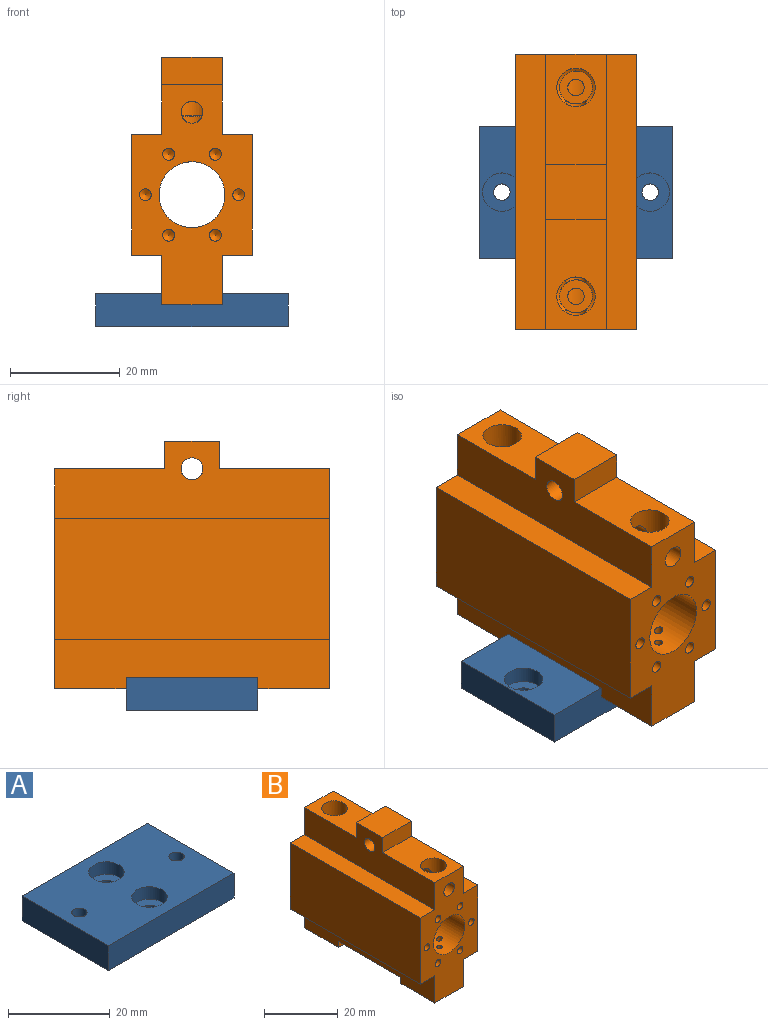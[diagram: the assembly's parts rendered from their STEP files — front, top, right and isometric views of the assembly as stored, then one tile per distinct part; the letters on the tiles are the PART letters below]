
ASSEMBLY  parts=2 mates=1
PART A: 18 faces, bbox 35x24x6 mm
  f0: plane 24x6mm, normal (-1,0,0), area 144mm2, adj f1,f3,f4,f5
  f1: plane 35x6mm, normal (0,-1,0), area 210mm2, adj f0,f2,f4,f5
  f2: plane 24x6mm, normal (1,0,0), area 144mm2, adj f1,f3,f4,f5
  f3: plane 35x6mm, normal (0,1,0), area 210mm2, adj f0,f2,f4,f5
  f4: plane 35x24mm, normal (0,0,1), area 748.9mm2, adj f0,f1,f2,f3,f8,f11,f12,f15
  f5: plane 35x24mm, normal (0,0,-1), area 748.9mm2, adj f0,f1,f2,f3,f6,f9,f14,f17
  f6: cylinder r=1.5mm len=3mm, axis (0,0,1), area 28.3mm2, adj f5,f7
  f7: plane 7x7mm, normal (0,0,1), area 31.4mm2, adj f6,f8
  f8: cylinder r=3.5mm len=7mm, axis (0,0,1), area 66mm2, adj f4,f7
  f9: cylinder r=1.5mm len=3mm, axis (0,0,1), area 28.3mm2, adj f5,f10
  f10: plane 7x7mm, normal (0,0,1), area 31.4mm2, adj f9,f11
  f11: cylinder r=3.5mm len=7mm, axis (0,0,1), area 66mm2, adj f4,f10
  f12: cylinder r=1.5mm len=3mm, axis (0,0,-1), area 28.3mm2, adj f4,f13
  f13: plane 7x7mm, normal (0,0,-1), area 31.4mm2, adj f12,f14
  f14: cylinder r=3.5mm len=7mm, axis (0,0,-1), area 66mm2, adj f5,f13
  f15: cylinder r=1.5mm len=3mm, axis (0,0,-1), area 28.3mm2, adj f4,f16
  f16: plane 7x7mm, normal (0,0,-1), area 31.4mm2, adj f15,f17
  f17: cylinder r=3.5mm len=7mm, axis (0,0,-1), area 66mm2, adj f5,f16
PART B: 77 faces, bbox 22x50x45 mm
  f0: cylinder r=0.75mm len=6.5mm, axis (0,0,-1), area 27.1mm2, adj f22,f76
  f1: cylinder r=0.75mm len=5.75mm, axis (0,0,-1), area 25mm2, adj f22,f76
  f2: cylinder r=0.75mm len=6.5mm, axis (0,0,-1), area 27.1mm2, adj f22,f76
  f3: cylinder r=0.75mm len=5.75mm, axis (0,0,-1), area 25mm2, adj f22,f76
  f4: cylinder r=0.75mm len=6.5mm, axis (0,0,-1), area 27.1mm2, adj f21,f76
  f5: cylinder r=0.75mm len=5.75mm, axis (0,0,-1), area 25mm2, adj f21,f76
  f6: cylinder r=0.75mm len=6.5mm, axis (0,0,-1), area 27.1mm2, adj f21,f76
  f7: cylinder r=0.75mm len=5.75mm, axis (0,0,-1), area 25mm2, adj f21,f76
  f8: cylinder r=1.5mm len=4.19mm, axis (0,0,1), area 38.6mm2, adj f68,f76
  f9: cylinder r=1.5mm len=4.19mm, axis (0,0,1), area 38.6mm2, adj f69,f76
  f10: plane 20x11mm, normal (0,0,1), area 181.5mm2, adj f12,f23,f31,f34,f72
  f11: cone r=0mm half-angle=59deg, axis (0,0,1), area 9.6mm2, adj f12,f17,f70
  f12: cylinder r=3.5mm len=7mm, axis (0,0,1), area 112.3mm2, adj f10,f11,f70
  f13: cone r=0mm half-angle=59deg, axis (0,0,1), area 3.6mm2, adj f15,f16,f70,f71
  f14: cone r=0mm half-angle=59deg, axis (0,0,1), area 3.6mm2, adj f15,f16,f70,f71
  f15: cylinder r=3.5mm len=7mm, axis (0,0,1), area 103.6mm2, adj f13,f14,f32,f70,f71
  f16: cylinder r=3mm len=6mm, axis (0,0,1), area 72.5mm2, adj f13,f14,f68,f70,f71
  f17: cylinder r=3mm len=6mm, axis (0,0,1), area 75.8mm2, adj f11,f69,f70
  f18: plane 13x11mm, normal (0,0,-1), area 104.5mm2, adj f19,f20,f33,f36,f38
  f19: plane 50x9mm, normal (-1,0,0), area 402mm2, adj f18,f26,f27,f33,f34,f37,f38,f39
  f20: plane 50x9mm, normal (1,0,0), area 402mm2, adj f18,f27,f28,f33,f34,f37,f38,f39
  f21: cone r=0mm half-angle=59deg, axis (0,0,-1), area 36.6mm2, adj f4,f5,f6,f7,f35
  f22: cone r=0mm half-angle=59deg, axis (0,0,-1), area 36.6mm2, adj f0,f1,f2,f3,f36
  f23: plane 50x14mm, normal (-1,0,0), area 487.4mm2, adj f10,f24,f32,f33,f34,f72,f73,f74
  f24: plane 50x5.5mm, normal (0,0,1), area 275mm2, adj f23,f25,f33,f34
  f25: plane 50x22mm, normal (-1,0,0), area 1100mm2, adj f24,f26,f33,f34
  f26: plane 50x5.5mm, normal (0,0,-1), area 275mm2, adj f19,f25,f33,f34
  f27: plane 13x11mm, normal (0,0,-1), area 104.5mm2, adj f19,f20,f34,f35,f37
  f28: plane 50x5.5mm, normal (0,0,-1), area 275mm2, adj f20,f29,f33,f34
  f29: plane 50x22mm, normal (1,0,0), area 1100mm2, adj f28,f30,f33,f34
  f30: plane 50x5.5mm, normal (0,0,1), area 275mm2, adj f29,f31,f33,f34
  f31: plane 50x14mm, normal (1,0,0), area 487.4mm2, adj f10,f30,f32,f33,f34,f72,f73,f74
  f32: plane 20x11mm, normal (0,0,1), area 181.5mm2, adj f15,f23,f31,f33,f73
  f33: plane 40x22mm, normal (0,-1,0), area 534.6mm2, adj f18,f19,f20,f23,f24,f25,f26,f28
  f34: plane 40x22mm, normal (0,1,0), area 547.1mm2, adj f10,f19,f20,f23,f24,f25,f26,f27
  f35: cylinder r=3.5mm len=8mm, axis (0,0,-1), area 175.9mm2, adj f21,f27
  f36: cylinder r=3.5mm len=8mm, axis (0,0,-1), area 175.9mm2, adj f18,f22
  f37: plane 11x2mm, normal (0,-1,0), area 22mm2, adj f19,f20,f27,f39
  f38: plane 11x2mm, normal (0,1,0), area 22mm2, adj f18,f19,f20,f39
  f39: plane 24x11mm, normal (0,0,-1), area 254.2mm2, adj f19,f20,f37,f38,f41,f43
  f40: cone r=0mm half-angle=59deg, axis (0,0,-1), area 5.7mm2, adj f41
  f41: cylinder r=1.25mm len=7mm, axis (0,0,-1), area 55mm2, adj f39,f40
  f42: cone r=0mm half-angle=59deg, axis (0,0,-1), area 5.7mm2, adj f43
  f43: cylinder r=1.25mm len=7mm, axis (0,0,-1), area 55mm2, adj f39,f42
  f44: cone r=0mm half-angle=59deg, axis (0,-1,0), area 4.2mm2, adj f45
  f45: cylinder r=1.07mm len=5mm, axis (0,-1,0), area 33.8mm2, adj f33,f44
  f46: cone r=0mm half-angle=59deg, axis (0,-1,0), area 4.2mm2, adj f47
  f47: cylinder r=1.07mm len=5mm, axis (0,-1,0), area 33.8mm2, adj f33,f46
  f48: cone r=0mm half-angle=59deg, axis (0,-1,0), area 4.2mm2, adj f49
  f49: cylinder r=1.07mm len=5mm, axis (0,-1,0), area 33.8mm2, adj f33,f48
  f50: cone r=0mm half-angle=59deg, axis (0,-1,0), area 4.2mm2, adj f51
  f51: cylinder r=1.07mm len=5mm, axis (0,-1,0), area 33.8mm2, adj f33,f50
  f52: cone r=0mm half-angle=59deg, axis (0,-1,0), area 4.2mm2, adj f53
  f53: cylinder r=1.07mm len=5mm, axis (0,-1,0), area 33.8mm2, adj f33,f52
  f54: cone r=0mm half-angle=59deg, axis (0,-1,0), area 4.2mm2, adj f55
  f55: cylinder r=1.07mm len=5mm, axis (0,-1,0), area 33.8mm2, adj f33,f54
  f56: cone r=0mm half-angle=59deg, axis (0,1,0), area 4.2mm2, adj f57
  f57: cylinder r=1.07mm len=5mm, axis (0,1,0), area 33.8mm2, adj f34,f56
  f58: cone r=0mm half-angle=59deg, axis (0,1,0), area 4.2mm2, adj f59
  f59: cylinder r=1.07mm len=5mm, axis (0,1,0), area 33.8mm2, adj f34,f58
  f60: cone r=0mm half-angle=59deg, axis (0,1,0), area 4.2mm2, adj f61
  f61: cylinder r=1.07mm len=5mm, axis (0,1,0), area 33.8mm2, adj f34,f60
  f62: cone r=0mm half-angle=59deg, axis (0,1,0), area 4.2mm2, adj f63
  f63: cylinder r=1.07mm len=5mm, axis (0,1,0), area 33.8mm2, adj f34,f62
  f64: cone r=0mm half-angle=59deg, axis (0,1,0), area 4.2mm2, adj f65
  f65: cylinder r=1.07mm len=5mm, axis (0,1,0), area 33.8mm2, adj f34,f64
  f66: cone r=0mm half-angle=59deg, axis (0,1,0), area 4.2mm2, adj f67
  f67: cylinder r=1.07mm len=5mm, axis (0,1,0), area 33.8mm2, adj f34,f66
  f68: plane 6x6mm, normal (0,0,1), area 21.2mm2, adj f8,f16
  f69: plane 6x6mm, normal (0,0,1), area 21.2mm2, adj f9,f17
  f70: cylinder r=2mm len=33.25mm, axis (0,-1,0), area 402.6mm2, adj f11,f12,f13,f14,f15,f16,f17
  f71: cylinder r=2mm len=4mm, axis (0,-1,0), area 38mm2, adj f13,f14,f15,f16,f33
  f72: plane 11x5mm, normal (0,1,0), area 55mm2, adj f10,f23,f31,f74
  f73: plane 11x5mm, normal (0,-1,0), area 55mm2, adj f23,f31,f32,f74
  f74: plane 11x10mm, normal (0,0,1), area 110mm2, adj f23,f31,f72,f73
  f75: cylinder r=2mm len=11mm, axis (-1,0,0), area 138.2mm2, adj f23,f31
  f76: cylinder r=6mm len=50mm, axis (0,-1,0), area 1855.9mm2, adj f0,f1,f2,f3,f4,f5,f6,f7
PLACE A rot(axis=(1,0,0),180deg) t=(-22.49,21.33,-4.35)mm
PLACE B t=(-4.99,34.33,13.65)mm
MATE fastened A.f5 <-> B.f39  axis (0,0,1) through (-4.99,9.33,-4.35)mm
